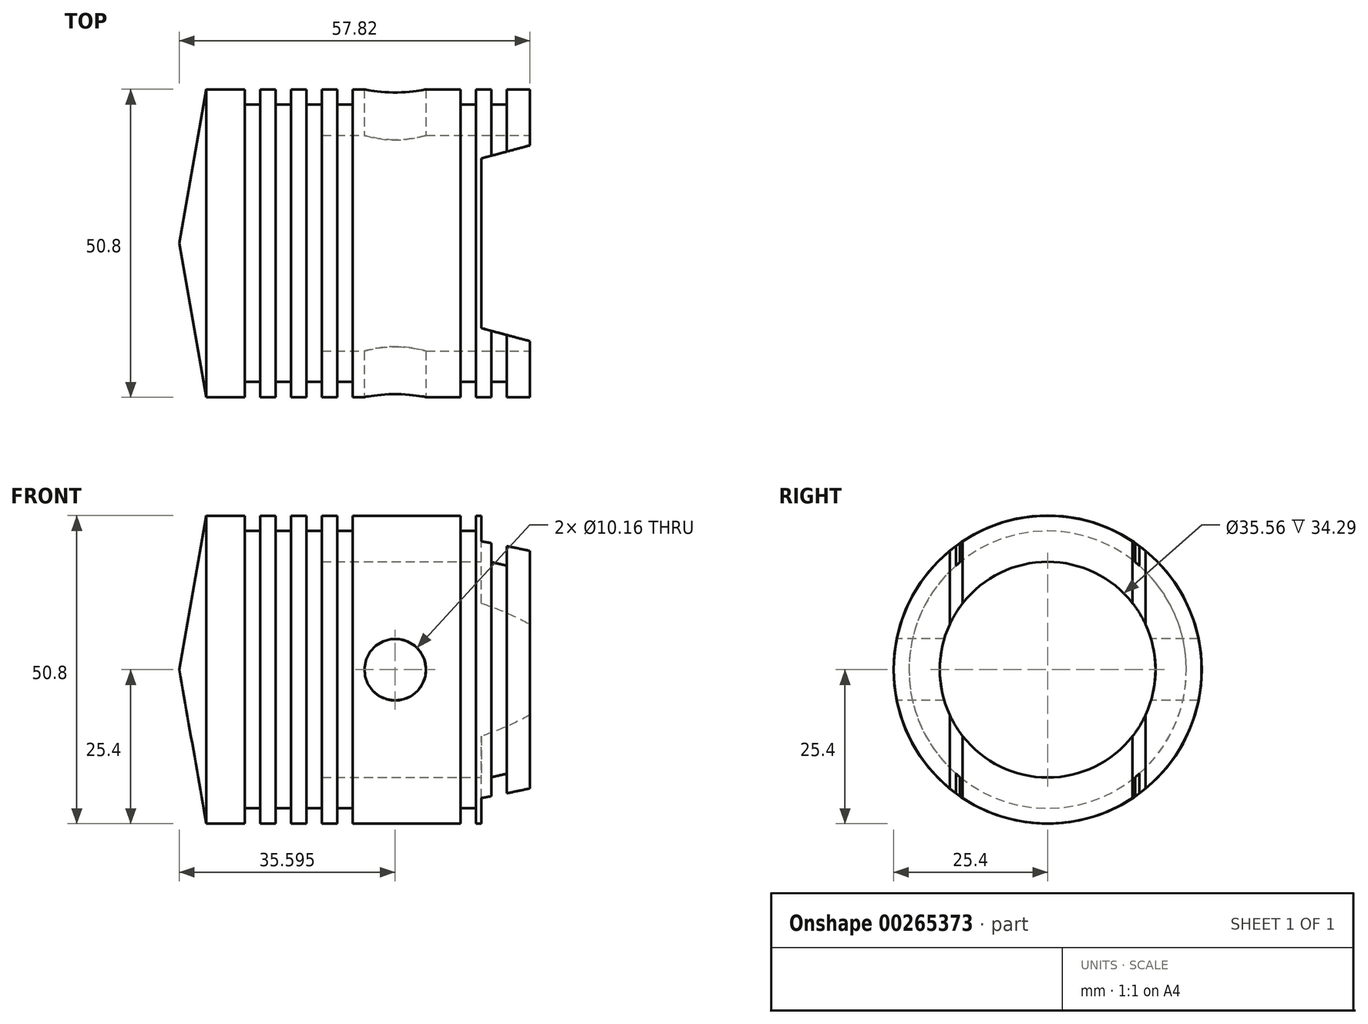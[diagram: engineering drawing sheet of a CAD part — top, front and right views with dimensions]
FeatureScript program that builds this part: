
annotation { "Feature Type Name" : "Feature", "Feature Type Description" : "" }
export const myFeature = defineFeature(function(context is Context, id is Id, definition is map)
    precondition{}
    {
        {
            var Q0;
            Q0=qCreatedBy(makeId("Front.planeOp"),FACE);
            var sketch = newSketch(context, id + "F0", { "sketchPlane" : qUnion([Q0])});
            skLineSegment(sketch, "E0", {"start": v(0, 0) * mm, "end": v(0, 25.4) * mm});
            skLineSegment(sketch, "E1", {"start": v(0, 25.4) * mm, "end": v(6.35, 25.4) * mm});
            skLineSegment(sketch, "E2", {"start": v(6.35, 25.4) * mm, "end": v(6.35, 22.86) * mm});
            skLineSegment(sketch, "E3", {"start": v(6.35, 22.86) * mm, "end": v(8.9, 22.86) * mm});
            skLineSegment(sketch, "E4", {"start": v(8.9, 22.86) * mm, "end": v(8.9, 25.4) * mm});
            skLineSegment(sketch, "E5", {"start": v(8.9, 25.4) * mm, "end": v(11.43, 25.4) * mm});
            skLineSegment(sketch, "E6", {"start": v(11.43, 25.4) * mm, "end": v(11.43, 22.86) * mm});
            skLineSegment(sketch, "E7", {"start": v(11.43, 22.86) * mm, "end": v(13.97, 22.86) * mm});
            skLineSegment(sketch, "E8", {"start": v(13.97, 22.86) * mm, "end": v(13.97, 25.4) * mm});
            skLineSegment(sketch, "E9", {"start": v(13.97, 25.4) * mm, "end": v(16.51, 25.4) * mm});
            skLineSegment(sketch, "E10", {"start": v(16.51, 25.4) * mm, "end": v(16.51, 22.86) * mm});
            skLineSegment(sketch, "E11", {"start": v(16.51, 22.86) * mm, "end": v(19.05, 22.86) * mm});
            skLineSegment(sketch, "E12", {"start": v(19.05, 22.86) * mm, "end": v(19.05, 25.4) * mm});
            skLineSegment(sketch, "E13", {"start": v(19.05, 25.4) * mm, "end": v(21.6, 25.4) * mm});
            skLineSegment(sketch, "E14", {"start": v(21.6, 25.4) * mm, "end": v(21.6, 22.86) * mm});
            skLineSegment(sketch, "E15", {"start": v(21.6, 22.86) * mm, "end": v(24.13, 22.86) * mm});
            skLineSegment(sketch, "E16", {"start": v(24.13, 22.86) * mm, "end": v(24.13, 25.4) * mm});
            skLineSegment(sketch, "E17", {"start": v(24.13, 25.4) * mm, "end": v(41.91, 25.4) * mm});
            skLineSegment(sketch, "E18", {"start": v(41.91, 25.4) * mm, "end": v(41.91, 22.86) * mm});
            skLineSegment(sketch, "E19", {"start": v(41.91, 22.86) * mm, "end": v(44.45, 22.86) * mm});
            skLineSegment(sketch, "E20", {"start": v(44.45, 22.86) * mm, "end": v(44.45, 25.4) * mm});
            skLineSegment(sketch, "E21", {"start": v(44.45, 25.4) * mm, "end": v(47, 25.4) * mm});
            skLineSegment(sketch, "E22", {"start": v(47, 25.4) * mm, "end": v(47, 22.86) * mm});
            skLineSegment(sketch, "E23", {"start": v(47, 22.86) * mm, "end": v(49.53, 22.86) * mm});
            skLineSegment(sketch, "E24", {"start": v(49.53, 22.86) * mm, "end": v(49.53, 25.4) * mm});
            skLineSegment(sketch, "E25", {"start": v(49.53, 25.4) * mm, "end": v(53.34, 25.4) * mm});
            skLineSegment(sketch, "E26", {"start": v(53.34, 25.4) * mm, "end": v(53.34, 25.37) * mm});
            skLineSegment(sketch, "E27", {"start": v(53.34, 25.37) * mm, "end": v(0, 25.37) * mm});
            skLineSegment(sketch, "E28", {"start": v(6.35, 25.4) * mm, "end": v(11.89, 25.4) * mm, "construction": true});
            skLineSegment(sketch, "E29", {"start": v(24.13, 25.4) * mm, "end": v(24.13, 22.86) * mm, "construction": true});
            skLineSegment(sketch, "E30", {"start": v(24.13, 22.86) * mm, "end": v(19.05, 22.86) * mm, "construction": true});
            skLineSegment(sketch, "E31", {"start": v(60.76, 22.86) * mm, "end": v(82.81, 22.86) * mm, "construction": true});
            skLineSegment(sketch, "E32", {"start": v(53.34, 25.4) * mm, "end": v(53.34, 17.78) * mm});
            skLineSegment(sketch, "E33", {"start": v(53.34, 17.78) * mm, "end": v(19.05, 17.78) * mm});
            skLineSegment(sketch, "E34.trimOffspring", {"start": v(8.9, 25.4) * mm, "end": v(11.43, 25.4) * mm, "construction": true});
            skLineSegment(sketch, "E35.trimOffspring", {"start": v(13.97, 25.4) * mm, "end": v(16.51, 25.4) * mm, "construction": true});
            skLineSegment(sketch, "E36.trimOffspring", {"start": v(19.05, 25.4) * mm, "end": v(21.6, 25.4) * mm, "construction": true});
            skLineSegment(sketch, "E37", {"start": v(19.05, 17.78) * mm, "end": v(19.05, 0) * mm});
            skLineSegment(sketch, "E38", {"start": v(19.05, 0) * mm, "end": v(0, 0) * mm});
            skLineSegment(sketch, "E39", {"start": v(0, 0) * mm, "end": v(-4.48, 0) * mm});
            skLineSegment(sketch, "E40", {"start": v(-4.48, 0) * mm, "end": v(0, 25.4) * mm});
            skSolve(sketch);
        }
        {
            var Q0;
            {var subQ25=sQuery(id+"F0.wireOp",EDGE,"E3");Q0=makeQuery(id+"F0.imprint","IMPRINT",FACE,{"disambiguationData":[TD([[makeQuery(id+"F0.imprint","IMPRINT",EDGE,{"derivedFrom":subQ25}),-1.0]])]});}
            var Q1;
            {var subQ0=sQuery(id+"F0.wireOp",EDGE,"E39");Q1=makeQuery(id+"F0.imprint","IMPRINT",FACE,{"disambiguationData":[TD([[makeQuery(id+"F0.imprint","IMPRINT",EDGE,{"derivedFrom":subQ0}),-1.0]])]});}
            var Q2;
            Q2=sQuery(id+"F0.wireOp",EDGE,"E38");
            revolve(context, id + "F1", {"entities" : qUnion([Q0, Q1]), "axis" : qUnion([Q2]), "revolveType" : RevolveType.FULL});
        }
        {
            var Q0;
            Q0=qCreatedBy(makeId("Front.planeOp"),FACE);
            var sketch = newSketch(context, id + "F2", { "sketchPlane" : qUnion([Q0])});
            skCircle(sketch, "E41", {"center": v(31.12, 0) * mm, "radius": 5.08 * mm});
            skSolve(sketch);
        }
        {
            var Q0;
            Q0 = qSketchRegion(id + "F2", true);
            extrude(context, id + "F3", {"entities" : qUnion([Q0]), "operationType" : NewBodyOperationType.REMOVE, "oppositeDirection" : true, "depth" : 127 * mm, "symmetric" : true});
        }
        {
            var Q0;
            Q0=qCreatedBy(makeId("Top.planeOp"),FACE);
            var sketch = newSketch(context, id + "F4", { "sketchPlane" : qUnion([Q0])});
            skLineSegment(sketch, "E42.0", {"start": v(53.34, 25.37) * mm, "end": v(53.34, -25.37) * mm});
            skLineSegment(sketch, "E43", {"start": v(53.34, -16.14) * mm, "end": v(45.34, -14) * mm});
            skLineSegment(sketch, "E44", {"start": v(45.34, -14) * mm, "end": v(45.34, 14) * mm});
            skLineSegment(sketch, "E45", {"start": v(45.34, 14) * mm, "end": v(53.34, 16.14) * mm});
            skSolve(sketch);
        }
        {
            var Q0;
            Q0 = qSketchRegion(id + "F4", true);
            extrude(context, id + "F5", {"entities" : qUnion([Q0]), "operationType" : NewBodyOperationType.REMOVE, "oppositeDirection" : true, "depth" : 100 * mm, "symmetric" : true});
        }
    });
